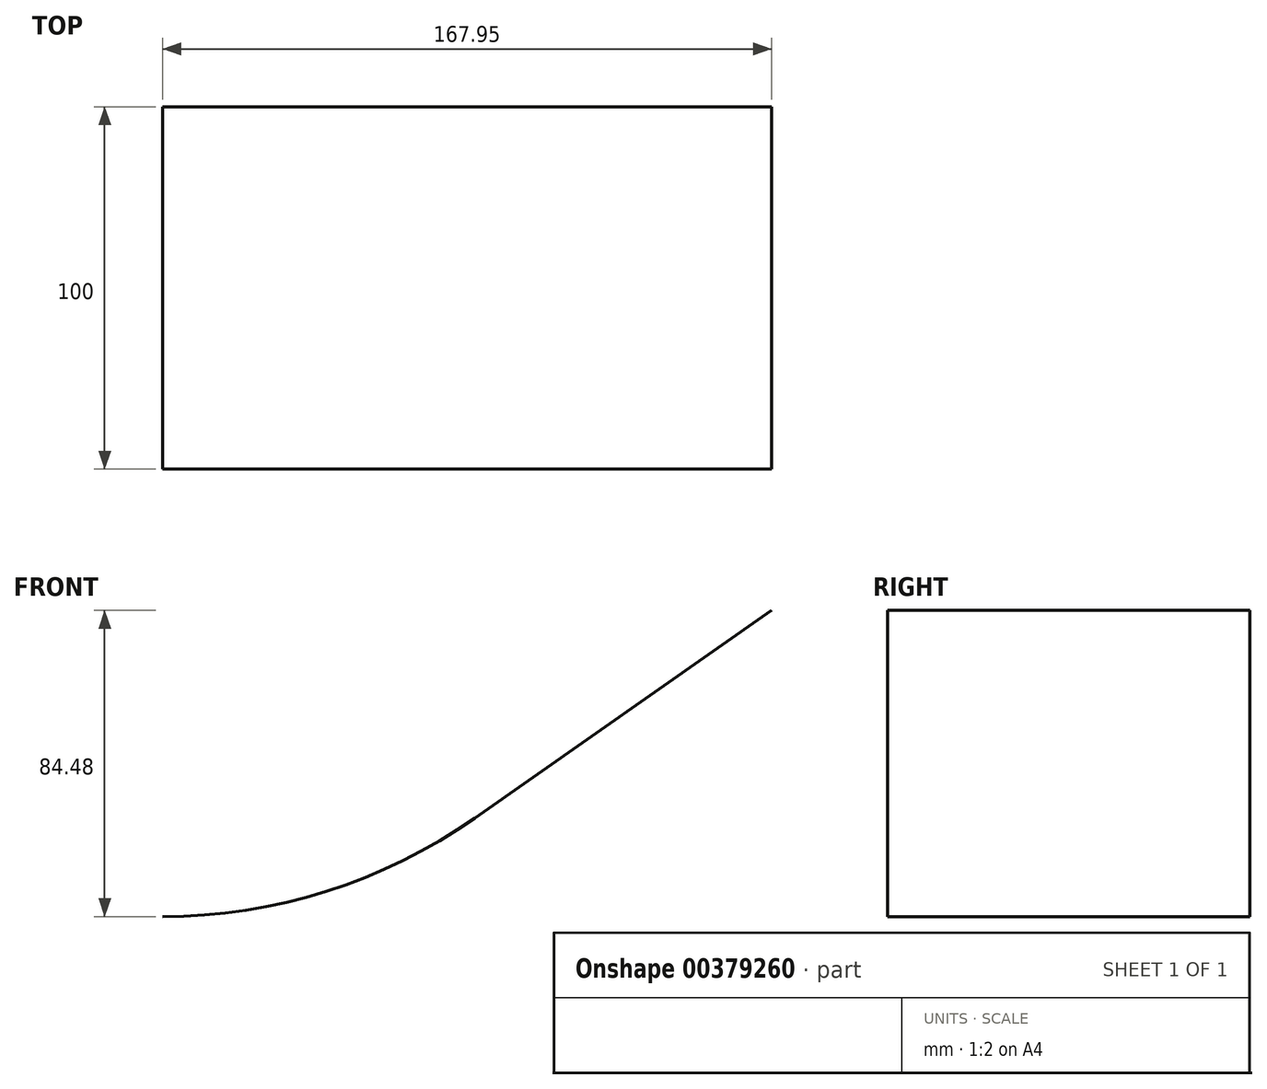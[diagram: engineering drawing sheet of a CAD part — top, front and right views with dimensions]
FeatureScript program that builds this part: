
annotation { "Feature Type Name" : "Feature", "Feature Type Description" : "" }
export const myFeature = defineFeature(function(context is Context, id is Id, definition is map)
    precondition{}
    {
        {
            var Q0;
            Q0=qCreatedBy(makeId("Front.planeOp"),FACE);
            var sketch = newSketch(context, id + "F0", { "sketchPlane" : qUnion([Q0])});
            skLineSegment(sketch, "E0", {"start": v(0, 182.71) * mm, "end": v(0, -150) * mm, "construction": true});
            skLineSegment(sketch, "E1", {"start": v(0, 0) * mm, "end": v(86.04, -122.87) * mm, "construction": true});
            skArc(sketch, "E2", {"start": v(0, -150) * mm, "mid": v(45.1, -143.06) * mm, "end": v(86.04, -122.87) * mm});
            skLineSegment(sketch, "E3", {"start": v(86.04, -122.87) * mm, "end": v(167.95, -65.52) * mm});
            skSolve(sketch);
        }
        {
            var Q0;
            Q0=sQuery(id+"F0.wireOp",EDGE,"E3");
            var Q1;
            Q1=sQuery(id+"F0.wireOp",EDGE,"E2");
            extrude(context, id + "F1", {"bodyType" : ToolBodyType.SURFACE, "surfaceEntities" : qUnion([Q0, Q1]), "oppositeDirection" : true, "depth" : 100 * mm});
        }
    });
